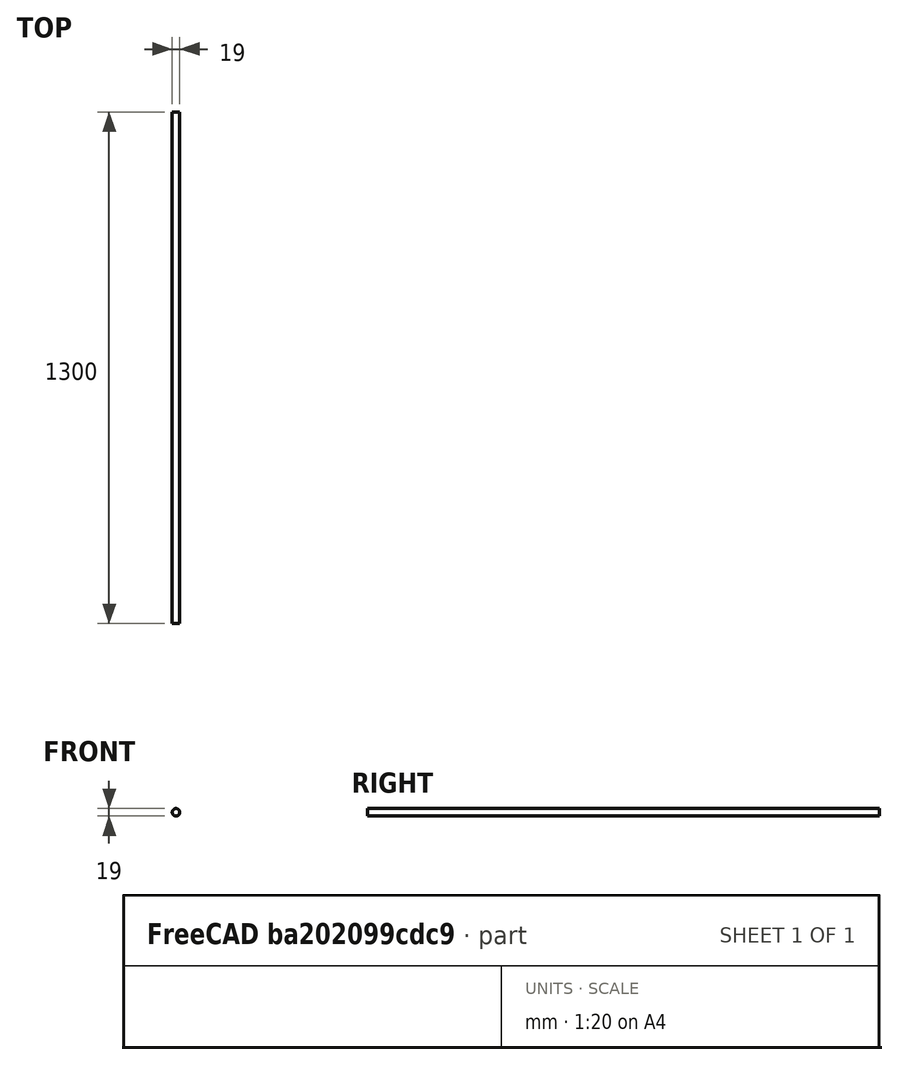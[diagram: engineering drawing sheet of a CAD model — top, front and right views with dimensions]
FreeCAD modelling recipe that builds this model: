
FCSTD DOCUMENT  (FreeCAD 0.17R10990 (Git))
Label: horizontal rod
License: All rights reserved
LicenseURL: http://en.wikipedia.org/wiki/All_rights_reserved
objects: Spreadsheet::Sheet×1, Sketcher::SketchObject×1, PartDesign::Pad×1
note: 3 computed .brp shape members not serialized (recipe doc carries the construction recipe); baked Part::Feature solids carry a one-line shape summary decoded from their .brp

FEATURE [Spreadsheet::Sheet] Spreadsheet  label="DImensions"
  cells = A1=base frame cross section; B1(baseframecrosssection)==50mm; A2=thickness; B2(thickness)==10mm; A3=inside thickness; B3(insidethickness)==B1 - 2 * B2; A4=base frame length; B4(baseframelength)==1100mm; A5=turn angle; B5(turnangle)==90deg; A6=distance of base frame support rod from origin; B6(distanceofbaseframesupportrodfromorigin)==200mm; A7=base frame support rod length; B7(baseframesupportrodlength)==1200mm; A8=distance between second base frame support rod; B8(distancebetweensecondbaseframesupportrod)==B4 - B6; A9=distance of vertical rods from origin; B9(distanceofverticalrodsfromorigin)==B16 * 0.5; A10=radius stopper rod pocket; B10(radiusstopperrodpocket)==20mm; A11=radius stopper rod; B11(radiusstopperrod)==B10 - 0.5mm; A12=half of base frame cross section; B12(halfofbaseframecrosssection)==B1 / 2; A13=base frame width; B13(baseframewidth)==1300mm; A14=half of base frame width; B14(halfofbaseframewidth)==B13 / 2; A15=stopper rod pocket depth; B15(stopperrodpocketdepth)==45mm; A16=length of collector frame; B16(lengthofcollectorframe)==2100mm; A17=height of stopper rod; B17(heightofstopperrod)==1850mm; A18=inner radius stopper rod; B18(innerradiusstopperrod)==B11 - B2; A19=height of hole at 30; B19(heightofholeat30)==606.93600000000004mm; A20=height of hole at 45; B20(heightofholeat45)==1050mm; A21=height of hole at 60; B21(heightofholeat60)==1816.5mm; A22=radius support rod horizontol pocket; B22(radiussupportrodhorizontolpocket)==10mm; A23=radius support rod horizontol; B23(radiussupportrodhorizontol)==B22 - 0.5mm; A24=collector frame length; B24(collectorframelength)==2100mm; A25=collector frame width; B25(collectorframewidth)==1100mm; A26=collector frame height; B26(collectorframeheight)==100mm; A27=collector frame pocket depth; B27(collectorframepocketdepth)==B26 - B2; A28=collector frame width after cut; B28(collectorframewidthaftercut)==150mm; A29=collector frame pocket inner width; B29(collectorframepocketinnerwidth)==B28 - B2; A30=collector frame plane offset; B30(collectorframeplaneoffset)==-B1 / 2; A31=collector frame x distance from origin; B31(collectorframexdistancefromorigin)==(B13 - B25 - B1) / 2; A32=collector frame pocket width; B32(collectorframepocketwidth)==B25 - B2; A33=collector frame pocket length; B33(collectorframepocketlength)==B24 - B2; A34=distance of second vertical rod from origin; B34(distanceofsecondverticalrodfromorigin)==B13 - B12; A35=support pin pocket radius; B35(supportpinpocketradius)==10mm; A36=support pin pocket x distance from origin; B36(supportpinpocketxdistancefromorigin)==50mm; A37=support pin radius; B37(supportpinradius)==9.5mm; A38=half of support pin length; B38(halfofsupportpinlength)==20mm
FEATURE [Sketcher::SketchObject] Sketch
  MapMode = 5
  Placement = pos=(0,0,0) rot=(1,0,0;1.5708rad)
  expr: Constraints[1] = Spreadsheet.radiussupportrodhorizontol
  sketch-geometry (1):
    g0: Circle CenterX=0 CenterY=0 CenterZ=0 NormalX=0 NormalY=0 NormalZ=1 Radius=9.5
  constraints (2):
    c: Coincident(g0,g-1)
    c: Radius(g0) = 9.5
FEATURE [PartDesign::Pad] Pad
  Length = 1300
  Length2 = 100
  Placement = pos=(0,0,0) rot=(1,0,0;1.5708rad)
  Profile = -> Sketch
  Type = 0
  expr: Length = Spreadsheet.baseframewidth
